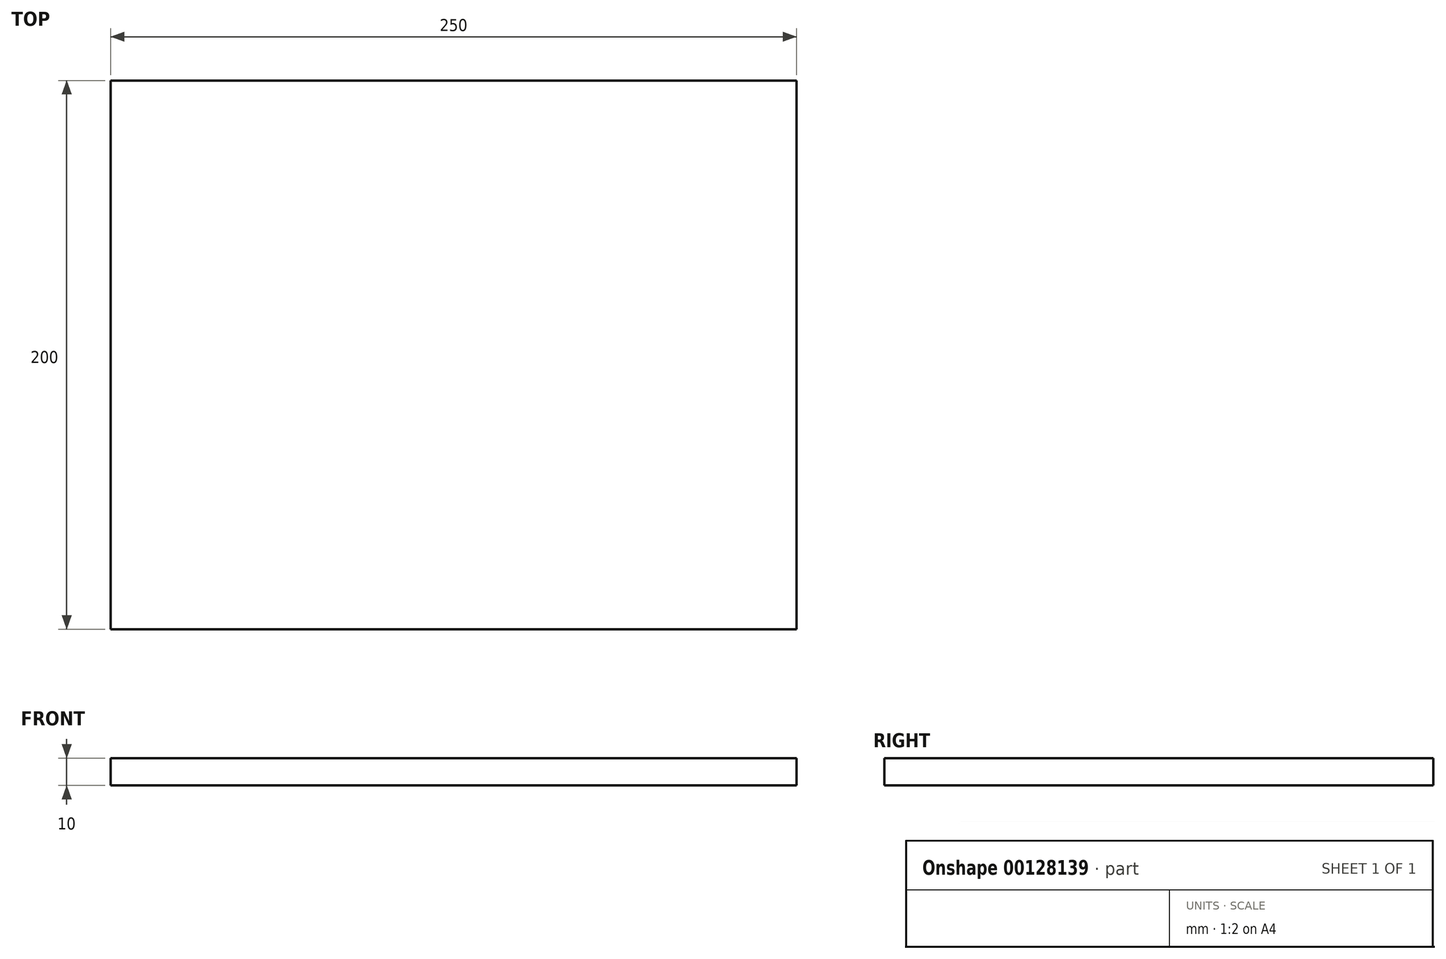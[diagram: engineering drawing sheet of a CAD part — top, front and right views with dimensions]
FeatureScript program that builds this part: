
annotation { "Feature Type Name" : "Feature", "Feature Type Description" : "" }
export const myFeature = defineFeature(function(context is Context, id is Id, definition is map)
    precondition{}
    {
        {
            var Q0;
            Q0=qCreatedBy(makeId("Top.planeOp"),FACE);
            var sketch = newSketch(context, id + "F0", { "sketchPlane" : qUnion([Q0])});
            skLineSegment(sketch, "E0.bottom", {"start": v(0, 0) * mm, "end": v(250, 0) * mm});
            skLineSegment(sketch, "E0.top", {"start": v(0, 200) * mm, "end": v(250, 200) * mm});
            skLineSegment(sketch, "E0.left", {"start": v(0, 0) * mm, "end": v(0, 200) * mm});
            skLineSegment(sketch, "E0.right", {"start": v(250, 0) * mm, "end": v(250, 200) * mm});
            skSolve(sketch);
        }
        {
            var Q0;
            Q0 = qSketchRegion(id + "F0", true);
            extrude(context, id + "F1", {"entities" : qUnion([Q0]), "depth" : 10 * mm});
        }
    });
